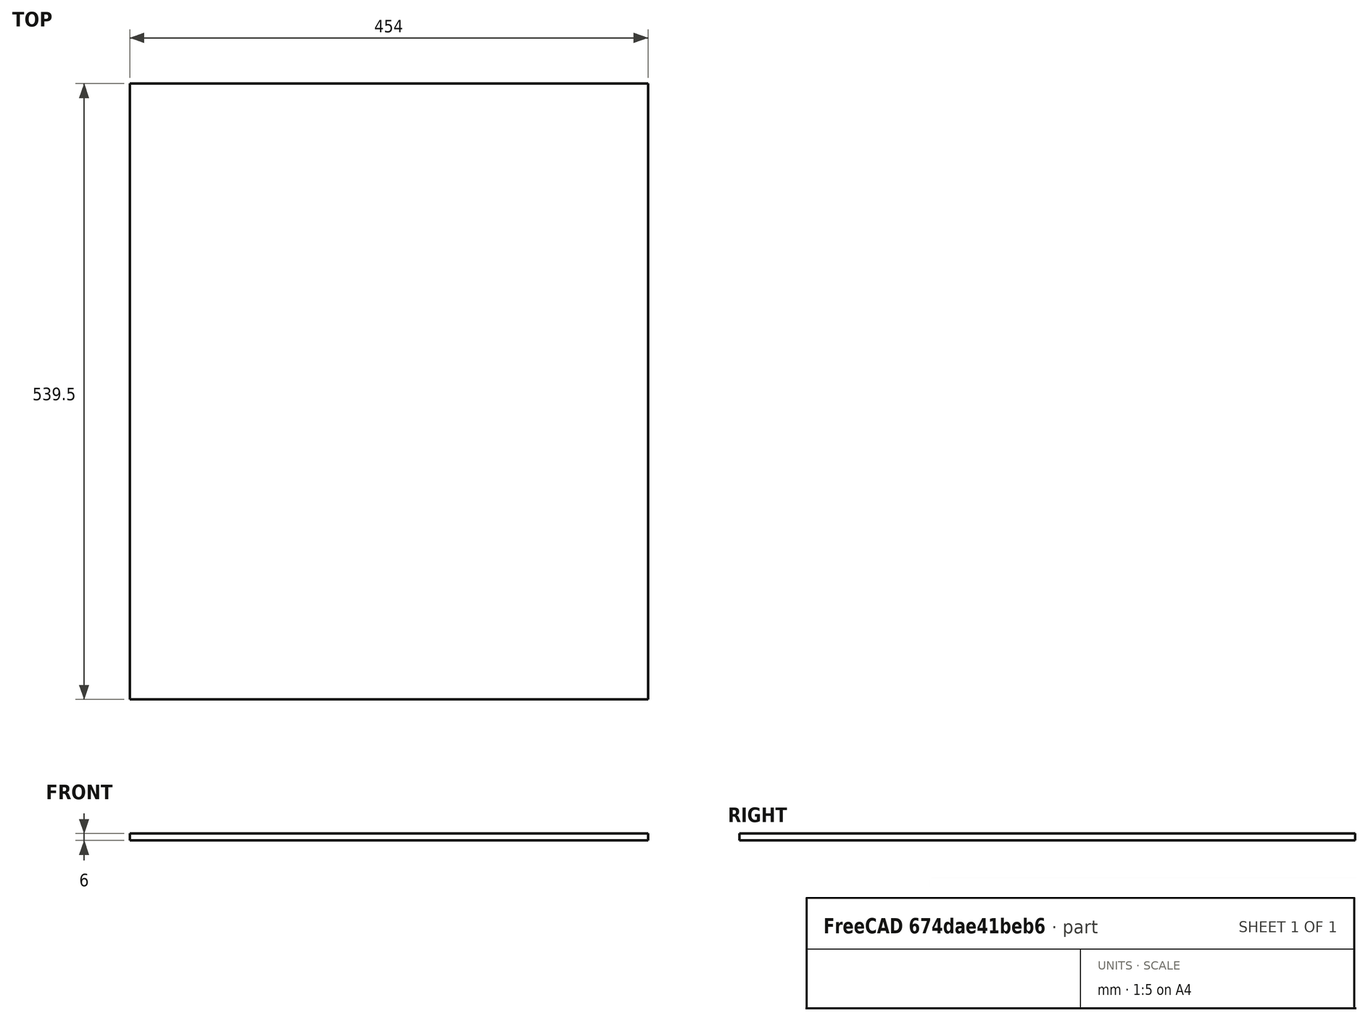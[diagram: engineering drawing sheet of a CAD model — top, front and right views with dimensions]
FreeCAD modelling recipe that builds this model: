
FCSTD DOCUMENT  (FreeCAD 1.0RUnknown)
Label: drawer_bottom
License: All rights reserved
objects: Sketcher::SketchObject×1, PartDesign::Pad×1, PartDesign::CoordinateSystem×1, PartDesign::Body×1
note: 7 computed .brp shape members not serialized (recipe doc carries the construction recipe); baked Part::Feature solids carry a one-line shape summary decoded from their .brp
EXTERNAL_REF file=../../mastersketch.FCStd obj=Spreadsheet

FEATURE [Sketcher::SketchObject] Sketch
  ArcFitTolerance = 1e-06
  AttachmentSupport = -> [XY_Plane]
  FullyConstrained = true
  MakeInternals = false
  MapMode = 5
  expr: Constraints[10] = mastersketch#Spreadsheet.drawer_width + 2 * (mastersketch#Spreadsheet.drawer_slot_depth + mastersketch#Spreadsheet.drawer_bottom_tol) - 2 * mastersketch#Spreadsheet.drawer_outer_thickness - 2
  expr: Constraints[11] = mastersketch#Spreadsheet.drawer_length + mastersketch#Spreadsheet.drawer_slot_depth + mastersketch#Spreadsheet.drawer_bottom_tol - mastersketch#Spreadsheet.drawer_outer_thickness
  sketch-geometry (5):
    g0: LineSegment StartX=-227 StartY=-269.75 StartZ=0 EndX=227 EndY=-269.75 EndZ=0
    g1: LineSegment StartX=227 StartY=-269.75 StartZ=0 EndX=227 EndY=269.75 EndZ=0
    g2: LineSegment StartX=227 StartY=269.75 StartZ=0 EndX=-227 EndY=269.75 EndZ=0
    g3: LineSegment StartX=-227 StartY=269.75 StartZ=0 EndX=-227 EndY=-269.75 EndZ=0
    g4: GeomPoint [constr] X=0 Y=0 Z=0
  constraints (12):
    c: Coincident(g0,g1)
    c: Coincident(g1,g2)
    c: Coincident(g2,g3)
    c: Coincident(g3,g0)
    c: Horizontal(g0)
    c: Horizontal(g2)
    c: Vertical(g1)
    c: Vertical(g3)
    c: Symmetric(g2,g0,g4)
    c: Coincident(g4,g-1)
    c: DistanceX(g0,g0) = 454
    c: DistanceY(g1,g1) = 539.5
FEATURE [PartDesign::Pad] Pad
  Direction = (0,0,1)
  Length = 6
  Length2 = 10
  Profile = -> Sketch
  ReferenceAxis = -> Sketch [N_Axis]
  Refine = true
  Suppressed = false
  Type = 0
  expr: Length = mastersketch#Spreadsheet.drawer_bottom_thickness
FEATURE [PartDesign::CoordinateSystem] LCS_front
  AttacherType = Attacher::AttachEngine3D
  AttachmentSupport = -> [Pad]
  MapMode = 45
  Placement = pos=(0,-269.75,0) rot=(0.57735,0.57735,0.57735;2.0944rad)
FEATURE [PartDesign::Body] Body  label="drawer_bottom"
  AllowCompound = false
  Group = -> [Sketch,Pad,LCS_front]
  Origin = -> Origin
  Tip = -> Pad
